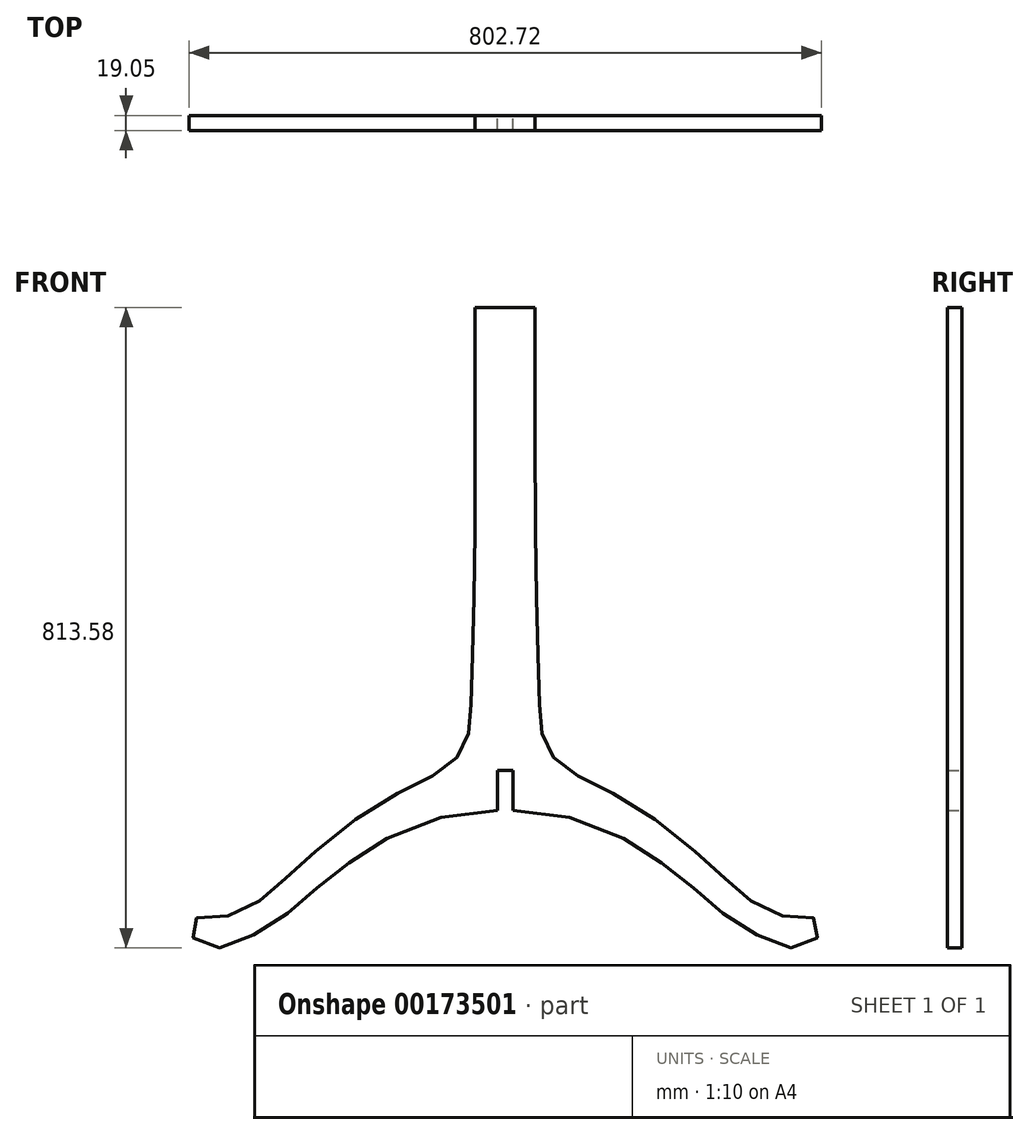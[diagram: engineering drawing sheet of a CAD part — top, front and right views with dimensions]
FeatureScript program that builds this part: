
annotation { "Feature Type Name" : "Feature", "Feature Type Description" : "" }
export const myFeature = defineFeature(function(context is Context, id is Id, definition is map)
    precondition{}
    {
        {
            var Q0;
            Q0=qCreatedBy(makeId("Front.planeOp"),FACE);
            var sketch = newSketch(context, id + "F0", { "sketchPlane" : qUnion([Q0])});
            skFitSpline(sketch, "E0", {"points": [v(23.88, -452.46) * mm, v(-43.93, -457.1) * mm, v(-117.64, -480.37) * mm, v(-164.88, -508.29) * mm, v(-192.84, -528.9) * mm, v(-221.64, -551.68) * mm, v(-247.01, -573.58) * mm, v(-273.67, -595.06) * mm, v(-305.06, -612.68) * mm, v(-332.99, -624.27) * mm, v(-357.85, -626.4) * mm, v(-374.14, -617.84) * mm, v(-381, -609.28) * mm, v(-381.85, -594.3) * mm, v(-371.14, -588.72) * mm, v(-348.85, -587.43) * mm, v(-328.27, -584.86) * mm, v(-304.26, -573.72) * mm, v(-279.4, -557.02) * mm, v(-262.25, -540.32) * mm, v(-239.53, -519.33) * mm, v(-202.23, -487.63) * mm, v(-153.36, -451.22) * mm, v(-110.48, -426.38) * mm, v(-80.05, -411.38) * mm, v(-61.19, -401.53) * mm, v(-45.32, -387.82) * mm, v(-34.18, -371.97) * mm, v(-29.46, -359.56) * mm, v(-26.03, -343.28) * mm, v(-25.17, -324) * mm, v(-24.32, -294.02) * mm, v(-21.98, -210.77) * mm, v(-20.23, -152.43) * mm, v(-19.65, 26.45) * mm], "startDerivative": vector(-1567.55, 26.46) * mm, "endDerivative": vector(-2.7, 3080.06) * mm});
            skLineSegment(sketch, "E1", {"start": v(-19.65, 26.45) * mm, "end": v(-19.65, 186.4) * mm});
            skLineSegment(sketch, "E2", {"start": v(18.45, 186.4) * mm, "end": v(18.45, -401.6) * mm, "construction": true});
            skLineSegment(sketch, "E3.MirrorCS", {"start": v(56.55, 26.45) * mm, "end": v(56.55, 186.4) * mm});
            skFitSpline(sketch, "E4.MirrorCS", {"points": [v(13.03, -452.46) * mm, v(80.83, -457.1) * mm, v(154.54, -480.37) * mm, v(201.78, -508.29) * mm, v(229.75, -528.9) * mm, v(258.55, -551.68) * mm, v(283.92, -573.58) * mm, v(310.58, -595.06) * mm, v(341.96, -612.68) * mm, v(369.9, -624.27) * mm, v(394.76, -626.4) * mm, v(411.05, -617.84) * mm, v(417.9, -609.28) * mm, v(418.75, -594.3) * mm, v(408.05, -588.72) * mm, v(385.75, -587.43) * mm, v(365.18, -584.86) * mm, v(341.17, -573.72) * mm, v(316.3, -557.02) * mm, v(299.15, -540.32) * mm, v(276.43, -519.33) * mm, v(239.14, -487.63) * mm, v(190.26, -451.22) * mm, v(147.4, -426.38) * mm, v(116.95, -411.38) * mm, v(98.1, -401.53) * mm, v(82.23, -387.82) * mm, v(71.08, -371.97) * mm, v(66.37, -359.56) * mm, v(62.94, -343.28) * mm, v(62.08, -324) * mm, v(61.22, -294.02) * mm, v(58.89, -210.77) * mm, v(57.13, -152.43) * mm, v(56.55, 26.45) * mm], "startDerivative": vector(1567.55, 26.46) * mm, "endDerivative": vector(2.7, 3080.06) * mm});
            skLineSegment(sketch, "E5", {"start": v(-19.65, 186.4) * mm, "end": v(56.55, 186.4) * mm});
            skLineSegment(sketch, "E6.0", {"start": v(28.1, -452.4) * mm, "end": v(28.1, -401.6) * mm});
            skLineSegment(sketch, "E7.0", {"start": v(8.8, -452.4) * mm, "end": v(8.8, -401.6) * mm});
            skLineSegment(sketch, "E8", {"start": v(8.8, -401.6) * mm, "end": v(28.1, -401.6) * mm});
            skLineSegment(sketch, "E9", {"start": v(28.1, -452.4) * mm, "end": v(28.1, -452.42) * mm});
            skLineSegment(sketch, "E10", {"start": v(8.8, -452.42) * mm, "end": v(8.8, -452.4) * mm});
            skPoint(sketch, "E11.orphan", {"position": v(18.45, -452.4) * mm});
            skPoint(sketch, "E12.orphan", {"position": v(8.8, -475.34) * mm});
            skLineSegment(sketch, "E13.trimOffspring", {"start": v(18.45, -452.4) * mm, "end": v(18.45, -779.66) * mm, "construction": true});
            skSolve(sketch);
        }
        {
            var Q0;
            {var subQ3=sQuery(id+"F0.wireOp",EDGE,"E1");Q0=makeQuery(id+"F0.imprint","IMPRINT",FACE,{"disambiguationData":[TD([[makeQuery(id+"F0.imprint","IMPRINT",EDGE,{"derivedFrom":subQ3}),-1.0]])]});}
            extrude(context, id + "F1", {"entities" : qUnion([Q0]), "depth" : 19.05 * mm});
        }
    });
